# Revit family: HUNTER_ACC-1200 Wall Mounted
name_source: partatom
category: Electrical Equipment
revit_build: Autodesk Revit 2017 (Build: 20160225_1515(x64)
units: mm (PartAtom-declared; Revit-internal decimal feet)

## family parameters
Cut with Voids When Loaded = No
Host = Face
OmniClass Number = 23.35.25.21
Panel Configuration = One Column
Part Type = Panelboard
Room Calculation Point = No
Round Connector Dimension = Use Diameter
Shared = Yes

## types (2) — shared parameters
Assembly Code = D5090900
Current = 2 A
Decoders = Expandable Up to 99 with Decoders
Default Elevation = 1200 mm
Enclosure_Depth = 160 mm  [stored 0.524934 ft]
Enclosure_Height = 310 mm  [stored 1.01706 ft]
Enclosure_Width = 390 mm  [stored 1.27953 ft]
Expansion Module = A2M-600 (6 Stations plug-in) Expansion Module
Input Voltage = 120 V
Keynote = 328423.04
Manufacturer = Hunter® Industries
Number of Sensor Inputs = 4+ Dedicated Flow Input
Output Voltage = 24 V
Panel Type = Modular
Power = 240 VA
Power factor = 1
Protection Rating = IP56
Sensor Input = 4 + Flow
Transformer Output = 24VAC, 4.0A
Type Comments = Hunter's Flagship Controller
Type Image = <None>
URL = https://www.hunterindustries.com
Voltage = 120

## per-type parameters (varying)
| type | Description | Enclosure Material | Model | Stations |
| ACC-1200 | 12-Station base unit , Wall mounted controller, expandable to 42 stations, with Metal Cabinet | Hunter® Metal Grey | ACC-1200 / ACC-1800 / ACC- 2400 / ACC-3000 / ACC-3600 / ACC-4200 | 12 Stations base count expandable to 42 Stations |
| ACC-1200-SS | 12-Station base unit , Wall mounted controller, expandable to 42 stations, with Stainless Steel Cabinet | Hunter® Stainless Steel | ACC-1200-SS / ACC-1800-SS / ACC- 2400-SS / ACC-3000-SS / ACC-3600-SS / ACC-4200-SS | 12 Stations base unit controller expandable to 42 Stations |

note: [stored X ft] marks values corroborated as IEEE doubles in the binary element streams (Revit-internal decimal feet)

## geometry (parser evidence)
native form markers: Sweep x4
no freeform markers — native parametric forms only
